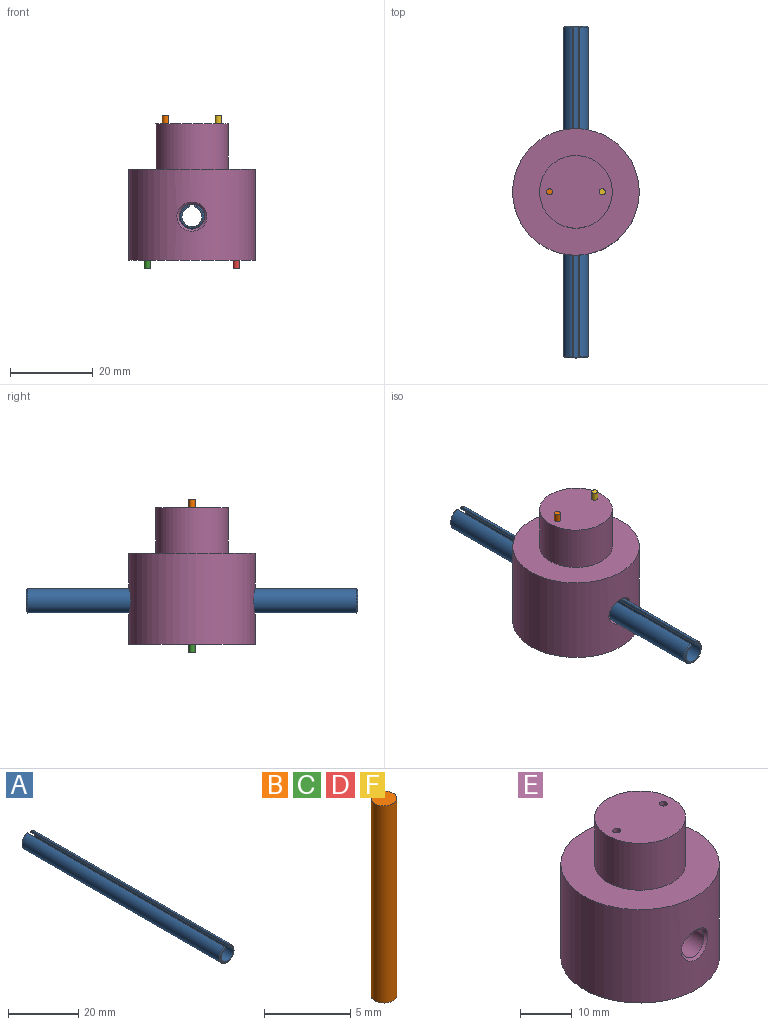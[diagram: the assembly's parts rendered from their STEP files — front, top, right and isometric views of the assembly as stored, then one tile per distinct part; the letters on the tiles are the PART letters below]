
ASSEMBLY  parts=6 mates=5
PART A: 8 faces, bbox 6x80x5.9 mm
  f0: cylinder r=3mm len=79.4mm, axis (0,1,0), area 1371.9mm2, adj f4,f5,f6,f7
  f1: plane 5.4x5.31mm, normal (0,-1,0), area 4.4mm2, adj f3,f4,f6,f7
  f2: plane 5.4x5.31mm, normal (0,1,0), area 4.4mm2, adj f3,f5,f6,f7
  f3: cylinder r=2.4mm len=80mm, axis (0,1,0), area 1105.8mm2, adj f1,f2,f6,f7
  f4: cone r=2.7mm half-angle=45deg, axis (0,1,0), area 7mm2, adj f0,f1,f6,f7
  f5: cone r=3mm half-angle=45deg, axis (0,-1,0), area 7mm2, adj f0,f2,f6,f7
  f6: plane 80x0.58mm, normal (-0.97,0,0.26), area 47.9mm2, adj f0,f1,f2,f3,f4,f5
  f7: plane 80x0.58mm, normal (0.97,0,0.26), area 47.9mm2, adj f0,f1,f2,f3,f4,f5
PART B: 3 faces, bbox 1.5x1.5x14 mm
  f0: cylinder r=0.75mm len=14mm, axis (0,0,-1), area 66mm2, adj f1,f2
  f1: plane 1.5x1.5mm, normal (0,0,1), area 1.8mm2, adj f0
  f2: plane 1.5x1.5mm, normal (0,0,-1), area 1.8mm2, adj f0
PART C: same geometry as B
PART D: same geometry as B
PART E: 16 faces, bbox 30.5x30.5x33 mm
  f0: cylinder r=15.25mm len=30.5mm, axis (0,0,-1), area 2028mm2, adj f1,f2,f14,f15
  f1: plane 30.5x30.5mm, normal (0,0,1), area 490.1mm2, adj f0,f3
  f2: plane 30.5x30.5mm, normal (0,0,-1), area 727.1mm2, adj f0,f9,f11
  f3: cylinder r=8.75mm len=17.5mm, axis (0,0,-1), area 604.8mm2, adj f1,f4
  f4: plane 17.5x17.5mm, normal (0,0,1), area 237mm2, adj f3,f5,f7
  f5: cylinder r=0.75mm len=12mm, axis (0,0,1), area 56.5mm2, adj f4,f6
  f6: plane 1.5x1.5mm, normal (0,0,1), area 1.8mm2, adj f5
  f7: cylinder r=0.75mm len=12mm, axis (0,0,1), area 56.5mm2, adj f4,f8
  f8: plane 1.5x1.5mm, normal (0,0,1), area 1.8mm2, adj f7
  f9: cylinder r=0.75mm len=12mm, axis (0,0,-1), area 56.5mm2, adj f2,f10
  f10: plane 1.5x1.5mm, normal (0,0,-1), area 1.8mm2, adj f9
  f11: cylinder r=0.75mm len=12mm, axis (0,0,-1), area 56.5mm2, adj f2,f12
  f12: plane 1.5x1.5mm, normal (0,0,-1), area 1.8mm2, adj f11
  f13: cylinder r=3mm len=29.5mm, axis (0,-1,0), area 556.1mm2, adj f14,f15
  f14: bspline ~7.23x6.99mm, area 15.5mm2, adj f0,f13
  f15: bspline ~7.23x6.99mm, area 15.5mm2, adj f0,f13
PART F: same geometry as B
PLACE A t=(-14.54,41.5,8.91)mm
PLACE B t=(-20.89,1.5,19.33)mm
PLACE C t=(-25.24,1.5,-3.67)mm
PLACE D t=(-3.84,1.5,-3.67)mm
PLACE E t=(-14.54,1.5,-1.67)mm
PLACE F t=(-8.19,1.5,19.33)mm
MATE fastened B.f0 <-> E.f7  axis (0,0,-1) through (-20.89,1.5,19.33)mm
MATE fastened A.f0 <-> E.f13  axis (0,1,0) through (-14.54,1.5,8.91)mm
MATE fastened F.f0 <-> E.f5  axis (0,0,-1) through (-8.19,1.5,19.33)mm
MATE fastened C.f0 <-> E.f11  axis (0,0,1) through (-25.24,1.5,10.33)mm
MATE fastened D.f0 <-> E.f9  axis (0,0,1) through (-3.84,1.5,10.33)mm
